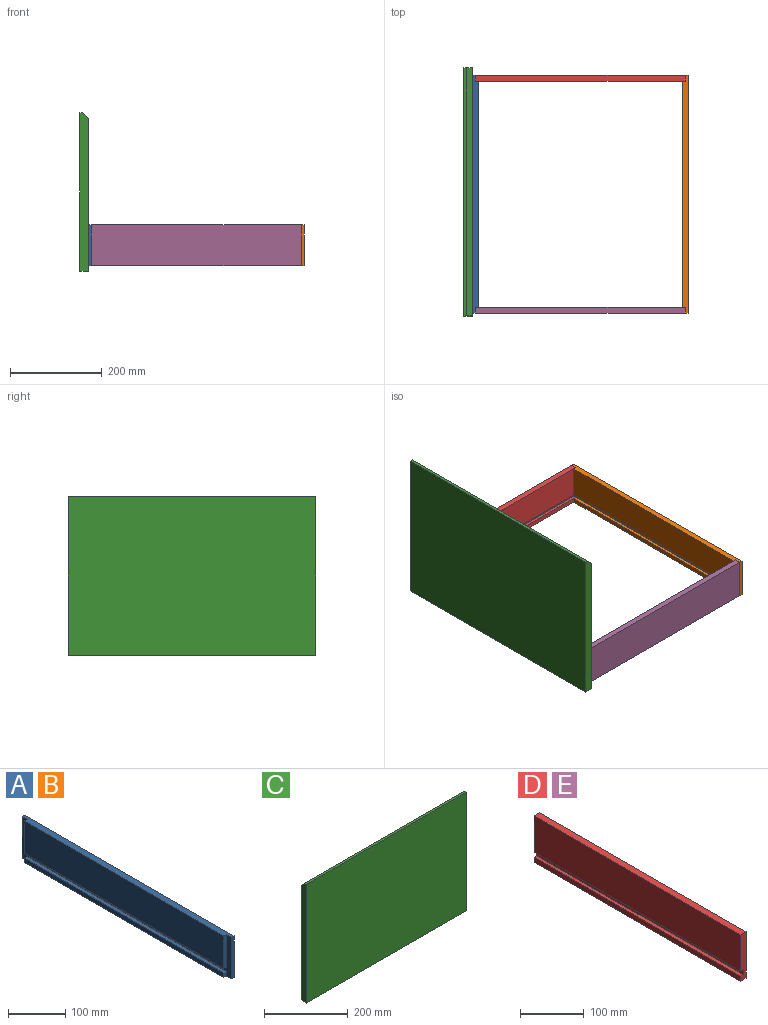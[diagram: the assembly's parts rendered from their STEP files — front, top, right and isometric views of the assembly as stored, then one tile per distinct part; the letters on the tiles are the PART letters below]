
ASSEMBLY  parts=5 mates=4
PART A: 14 faces, bbox 12.7x517.5x88.9 mm
  f0: plane 492.13x9.53mm, normal (-1,0,0), area 4687.5mm2, adj f6,f9,f10,f12
  f1: plane 69.85x6.35mm, normal (0,-1,0), area 443.5mm2, adj f3,f4,f11,f13
  f2: plane 69.85x6.35mm, normal (0,1,0), area 443.5mm2, adj f3,f4,f11,f13
  f3: plane 517.53x12.7mm, normal (0,0,1), area 6411.3mm2, adj f1,f2,f4,f5,f7,f8,f11
  f4: plane 492.13x69.85mm, normal (-1,0,0), area 34374.9mm2, adj f1,f2,f3,f13
  f5: plane 88.9x6.35mm, normal (0,-1,0), area 564.5mm2, adj f3,f6,f8,f11
  f6: plane 517.53x12.7mm, normal (0,0,-1), area 6411.3mm2, adj f0,f5,f7,f8,f9,f10,f11
  f7: plane 88.9x6.35mm, normal (0,1,0), area 564.5mm2, adj f3,f6,f8,f11
  f8: plane 517.53x88.9mm, normal (1,0,0), area 46008mm2, adj f3,f5,f6,f7
  f9: plane 9.53x6.35mm, normal (0,-1,0), area 60.5mm2, adj f0,f6,f11,f12
  f10: plane 9.53x6.35mm, normal (0,1,0), area 60.5mm2, adj f0,f6,f11,f12
  f11: plane 517.53x88.9mm, normal (-1,0,0), area 6945.6mm2, adj f1,f2,f3,f5,f6,f7,f9,f10
  f12: plane 492.13x6.35mm, normal (0,0,1), area 3125mm2, adj f0,f9,f10,f11
  f13: plane 492.13x6.35mm, normal (0,0,-1), area 3125mm2, adj f1,f2,f4,f11
PART B: same geometry as A
PART C: 7 faces, bbox 539.8x19.1x346.1 mm
  f0: plane 346.08x19.05mm, normal (-1,0,0), area 6512.1mm2, adj f1,f3,f4,f5,f6
  f1: plane 539.75x19.05mm, normal (0,0,-1), area 10282.2mm2, adj f0,f2,f4,f5
  f2: plane 346.08x19.05mm, normal (1,0,0), area 6512.1mm2, adj f1,f3,f4,f5,f6
  f3: plane 539.75x6.35mm, normal (0,0,1), area 3427.4mm2, adj f0,f2,f4,f6
  f4: plane 539.75x346.08mm, normal (0,-1,0), area 186794mm2, adj f0,f1,f2,f3
  f5: plane 539.75x333.38mm, normal (0,1,0), area 179939.2mm2, adj f0,f1,f2,f6
  f6: plane 539.75x12.7mm, normal (0,0.71,0.71), area 9694.2mm2, adj f0,f2,f3,f5
PART D: 10 faces, bbox 12.7x457.2x88.9 mm
  f0: plane 457.2x9.53mm, normal (-1,0,0), area 4354.8mm2, adj f1,f2,f3,f8
  f1: plane 88.9x12.7mm, normal (0,-1,0), area 1068.5mm2, adj f0,f2,f4,f5,f6,f7,f8,f9
  f2: plane 457.2x12.7mm, normal (0,0,-1), area 5806.4mm2, adj f0,f1,f3,f5
  f3: plane 88.9x12.7mm, normal (0,1,0), area 1068.5mm2, adj f0,f2,f4,f5,f6,f7,f8,f9
  f4: plane 457.2x12.7mm, normal (0,0,1), area 5806.4mm2, adj f1,f3,f5,f6
  f5: plane 457.2x88.9mm, normal (1,0,0), area 40645.1mm2, adj f1,f2,f3,f4
  f6: plane 457.2x69.85mm, normal (-1,0,0), area 31935.4mm2, adj f1,f3,f4,f7
  f7: plane 457.2x6.35mm, normal (0,0,-1), area 2903.2mm2, adj f1,f3,f6,f9
  f8: plane 457.2x6.35mm, normal (0,0,1), area 2903.2mm2, adj f0,f1,f3,f9
  f9: plane 457.2x9.53mm, normal (-1,0,0), area 4354.8mm2, adj f1,f3,f7,f8
PART E: same geometry as D
PLACE A rot(axis=(0,0,-1),180deg) t=(-330.3,257.51,182.53)mm
PLACE B t=(114.2,-260.02,182.53)mm
PLACE C rot(axis=(0,0,-1),90deg) t=(-343,273.38,169.83)mm
PLACE D rot(axis=(0,0,1),90deg) t=(120.55,244.81,182.53)mm
PLACE E rot(axis=(0,0,-1),90deg) t=(-336.65,-247.32,182.53)mm
MATE fastened B.f11 <-> D.f1  axis (-1,0,0) through (120.55,257.51,271.43)mm
MATE fastened A.f11 <-> D.f3  axis (1,0,0) through (-336.65,257.51,271.43)mm
MATE fastened E.f3 <-> B.f11  axis (1,0,0) through (120.55,-260.02,271.43)mm
MATE fastened C.f5 <-> A.f8  axis (1,0,0) through (-343,3.51,169.83)mm
